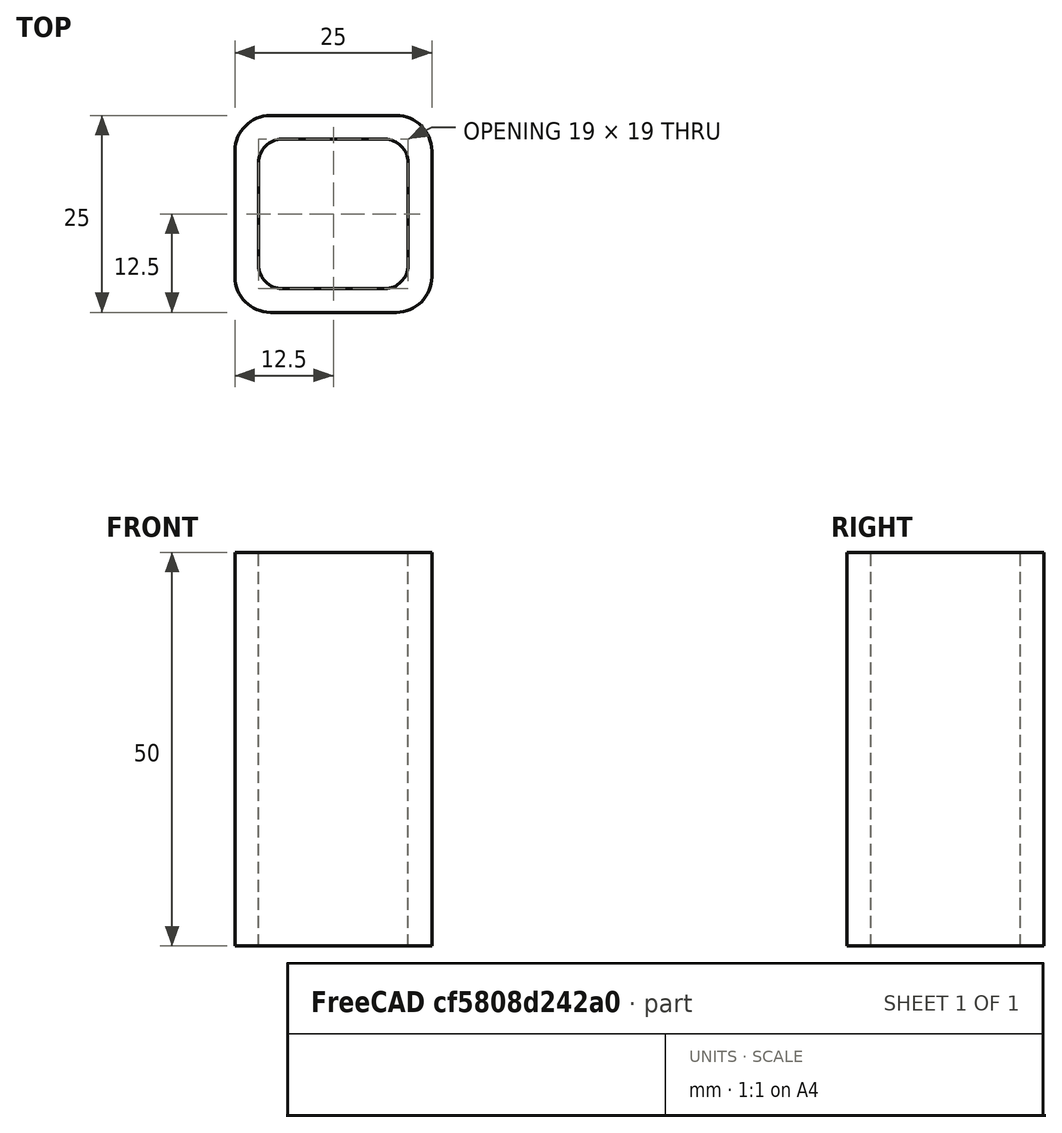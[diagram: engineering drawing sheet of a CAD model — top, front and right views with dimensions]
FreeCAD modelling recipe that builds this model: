
FCSTD DOCUMENT  (FreeCAD 0.15R4671 (Git))
Label: Square hollow section 25x25x3 EN10219 S235JRH
License: All rights reserved
LicenseURL: http://en.wikipedia.org/wiki/All_rights_reserved
objects: Sketcher::SketchObject×1, Part::Extrusion×1
note: 2 computed .brp shape members not serialized (recipe doc carries the construction recipe); baked Part::Feature solids carry a one-line shape summary decoded from their .brp

FEATURE [Sketcher::SketchObject] Sketch
  sketch-geometry (16):
    g0: LineSegment StartX=-6.5 StartY=9.5 StartZ=0 EndX=6.5 EndY=9.5 EndZ=0
    g1: LineSegment StartX=9.5 StartY=6.5 StartZ=0 EndX=9.5 EndY=-6.5 EndZ=0
    g2: LineSegment StartX=6.5 StartY=-9.5 StartZ=0 EndX=-6.5 EndY=-9.5 EndZ=0
    g3: LineSegment StartX=-9.5 StartY=-6.5 StartZ=0 EndX=-9.5 EndY=6.5 EndZ=0
    g4: LineSegment StartX=-8 StartY=12.5 StartZ=0 EndX=8 EndY=12.5 EndZ=0
    g5: LineSegment StartX=12.5 StartY=8 StartZ=0 EndX=12.5 EndY=-8 EndZ=0
    g6: LineSegment StartX=8 StartY=-12.5 StartZ=0 EndX=-8 EndY=-12.5 EndZ=0
    g7: LineSegment StartX=-12.5 StartY=-8 StartZ=0 EndX=-12.5 EndY=8 EndZ=0
    g8: ArcOfCircle CenterX=-6.5 CenterY=6.5 CenterZ=0 NormalX=0 NormalY=0 NormalZ=1 Radius=3 StartAngle=1.5708 EndAngle=3.14159
    g9: ArcOfCircle CenterX=6.5 CenterY=6.5 CenterZ=0 NormalX=0 NormalY=0 NormalZ=1 Radius=3 StartAngle=0 EndAngle=1.5708
    g10: ArcOfCircle CenterX=6.5 CenterY=-6.5 CenterZ=0 NormalX=0 NormalY=0 NormalZ=1 Radius=3 StartAngle=4.71239 EndAngle=6.28319
    g11: ArcOfCircle CenterX=-6.5 CenterY=-6.5 CenterZ=0 NormalX=0 NormalY=0 NormalZ=1 Radius=3 StartAngle=3.14159 EndAngle=4.71239
    g12: ArcOfCircle CenterX=8 CenterY=8 CenterZ=0 NormalX=0 NormalY=0 NormalZ=1 Radius=4.5 StartAngle=0 EndAngle=1.5708
    g13: ArcOfCircle CenterX=8 CenterY=-8 CenterZ=0 NormalX=0 NormalY=0 NormalZ=1 Radius=4.5 StartAngle=4.71239 EndAngle=6.28319
    g14: ArcOfCircle CenterX=-8 CenterY=-8 CenterZ=0 NormalX=0 NormalY=0 NormalZ=1 Radius=4.5 StartAngle=3.14159 EndAngle=4.71239
    g15: ArcOfCircle CenterX=-8 CenterY=8 CenterZ=0 NormalX=0 NormalY=0 NormalZ=1 Radius=4.5 StartAngle=1.5708 EndAngle=3.14159
  constraints (36):
    c: Horizontal(g2)
    c: Vertical(g3)
    c: Horizontal(g6)
    c: Vertical(g7)
    c: Tangent(g3,g8) = 1.5708
    c: Tangent(g0,g8) = 1.5708
    c: Tangent(g0,g9) = 1.5708
    c: Tangent(g1,g9) = 1.5708
    c: Tangent(g1,g10) = 1.5708
    c: Tangent(g2,g10) = 1.5708
    c: Tangent(g2,g11) = 1.5708
    c: Tangent(g3,g11) = 1.5708
    c: Tangent(g4,g12) = 1.5708
    c: Tangent(g5,g12) = 1.5708
    c: Tangent(g5,g13) = 1.5708
    c: Tangent(g6,g13) = 1.5708
    c: Tangent(g6,g14) = 1.5708
    c: Tangent(g7,g14) = 1.5708
    c: Tangent(g7,g15) = 1.5708
    c: Tangent(g4,g15) = 1.5708
    c: Equal(g9,g8)
    c: Equal(g9,g11)
    c: Equal(g9,g10)
    c: Equal(g12,g15)
    c: Equal(g12,g14)
    c: Equal(g12,g13)
    c: Symmetric(g4,g6,g-1)
    c: Symmetric(g7,g5,g-2)
    c: DistanceY(g4,g6) = -25
    c: DistanceX(g7,g5) = 25
    c: Symmetric(g3,g1,g-2)
    c: Symmetric(g0,g2,g-1)
    c: DistanceY(g0,g4) = 3
    c: DistanceX(g5,g1) = -3
    c: Radius(g9) = 3
    c: Radius(g12) = 4.5
FEATURE [Part::Extrusion] Extrude  label="Square hollow section 25x25x3 EN10219 S235JRH"
  Base = -> Sketch
  Dir = (0,0,50)
  Solid = true
